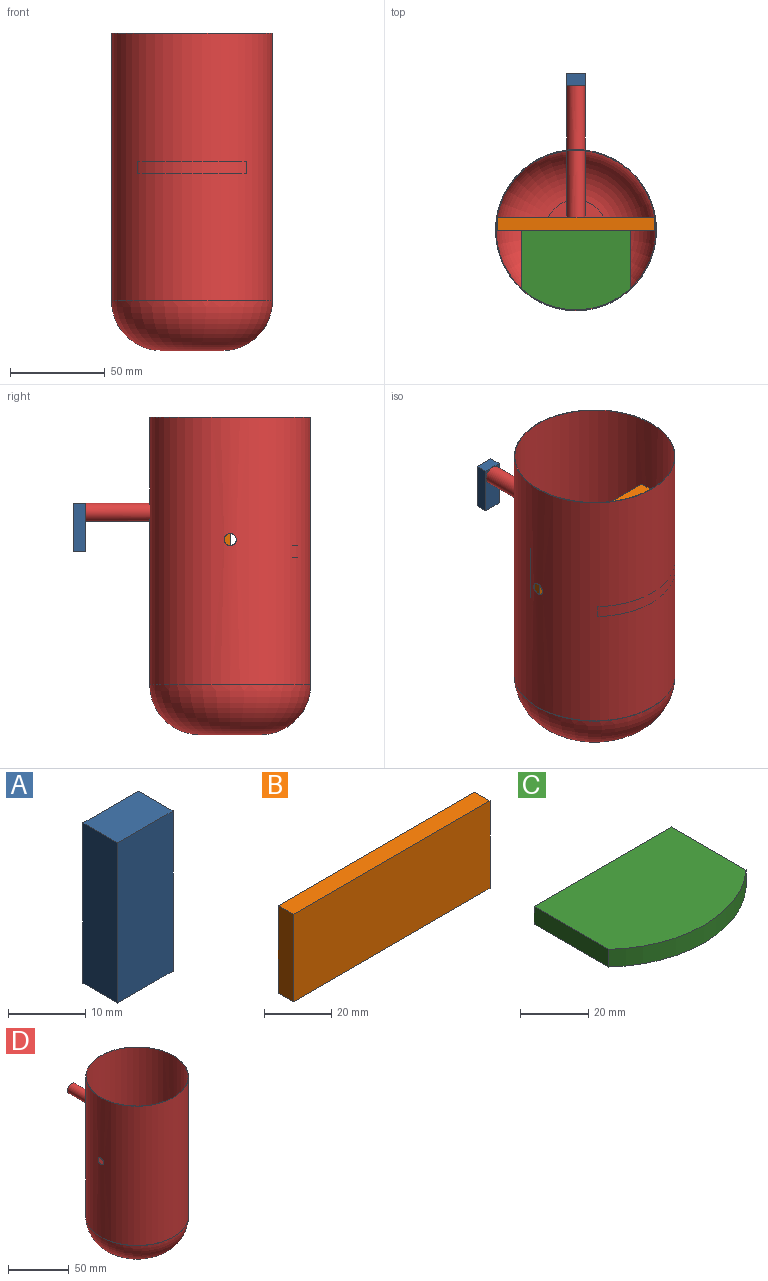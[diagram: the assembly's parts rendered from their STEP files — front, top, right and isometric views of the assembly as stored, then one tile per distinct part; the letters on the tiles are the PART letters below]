
ASSEMBLY  parts=4 mates=2
PART A: 6 faces, bbox 10.2x6.4x25.4 mm
  f0: plane 25.4x10.16mm, normal (0,-1,0), area 258.1mm2, adj f1,f3,f4,f5
  f1: plane 10.16x6.35mm, normal (0,0,-1), area 64.5mm2, adj f0,f2,f4,f5
  f2: plane 25.4x10.16mm, normal (0,1,0), area 258.1mm2, adj f1,f3,f4,f5
  f3: plane 10.16x6.35mm, normal (0,0,1), area 64.5mm2, adj f0,f2,f4,f5
  f4: plane 25.4x6.35mm, normal (-1,0,0), area 161.3mm2, adj f0,f1,f2,f3
  f5: plane 25.4x6.35mm, normal (1,0,0), area 161.3mm2, adj f0,f1,f2,f3
PART B: 6 faces, bbox 82.6x6.4x31.8 mm
  f0: plane 82.55x6.35mm, normal (0,0,1), area 524.2mm2, adj f1,f3,f4,f5
  f1: plane 31.75x6.35mm, normal (-1,0,0), area 201.6mm2, adj f0,f2,f4,f5
  f2: plane 82.55x6.35mm, normal (0,0,-1), area 524.2mm2, adj f1,f3,f4,f5
  f3: plane 31.75x6.35mm, normal (1,0,0), area 201.6mm2, adj f0,f2,f4,f5
  f4: plane 82.55x31.75mm, normal (0,1,0), area 2621mm2, adj f0,f1,f2,f3
  f5: plane 82.55x31.75mm, normal (0,-1,0), area 2621mm2, adj f0,f1,f2,f3
PART C: 6 faces, bbox 57.2x42.1x6.4 mm
  f0: cylinder r=42.07mm len=57.15mm, axis (0,0,-1), area 399mm2, adj f1,f2,f3,f4
  f1: plane 57.15x42.07mm, normal (0,0,-1), area 2203.8mm2, adj f0,f3,f4,f5
  f2: plane 57.15x42.07mm, normal (0,0,1), area 2203.8mm2, adj f0,f3,f4,f5
  f3: plane 30.87x6.35mm, normal (-1,0,0), area 196.1mm2, adj f0,f1,f2,f5
  f4: plane 30.87x6.35mm, normal (1,0,0), area 196.1mm2, adj f0,f1,f2,f5
  f5: plane 57.15x6.35mm, normal (0,1,0), area 362.9mm2, adj f1,f2,f3,f4
PART D: 13 faces, bbox 84.6x118.5x166.9 mm
  f0: cylinder r=42.32mm len=140.73mm, axis (0,0,-1), area 37288.9mm2, adj f2,f4,f9,f11,f12
  f1: cylinder r=42.07mm len=140.73mm, axis (0,0,-1), area 37064mm2, adj f2,f6,f8,f11,f12
  f2: plane 84.65x84.65mm, normal (0,0,1), area 67.3mm2, adj f0,f1
  f3: plane 32.23x32.23mm, normal (0,0,-1), area 815.7mm2, adj f4
  f4: torus R=16.11mm, axis (0,0,1), area 8484.2mm2, adj f0,f3
  f5: plane 32.23x32.23mm, normal (0,0,1), area 815.7mm2, adj f6
  f6: torus R=16.11mm, axis (0,0,1), area 8360.5mm2, adj f1,f5
  f7: plane 9.53x9.53mm, normal (0,-1,0), area 71.3mm2, adj f8
  f8: cylinder r=4.76mm len=42.07mm, axis (0,-1,0), area 1254.8mm2, adj f1,f7
  f9: cylinder r=4.76mm len=34.15mm, axis (0,-1,0), area 1017.8mm2, adj f0,f10
  f10: plane 9.53x9.53mm, normal (0,1,0), area 71.3mm2, adj f9
  f11: cylinder r=3.17mm len=6.35mm, axis (1,0,0), area 5.1mm2, adj f0,f1
  f12: cylinder r=3.17mm len=6.35mm, axis (-1,0,0), area 5.1mm2, adj f0,f1
PLACE A t=(-45.58,53.08,-83.22)mm
PLACE B t=(-45.33,53.31,-43.79)mm
PLACE C t=(-45.58,53.31,-43.67)mm
PLACE D t=(-45.58,53.31,-82.96)mm
MATE fastened D.f8 <-> A.f0  axis (0,1,0) through (-45.58,129.51,33.86)mm
MATE fastened C.f5 <-> B.f5  axis (0,1,0) through (-45.58,53.31,13.36)mm
